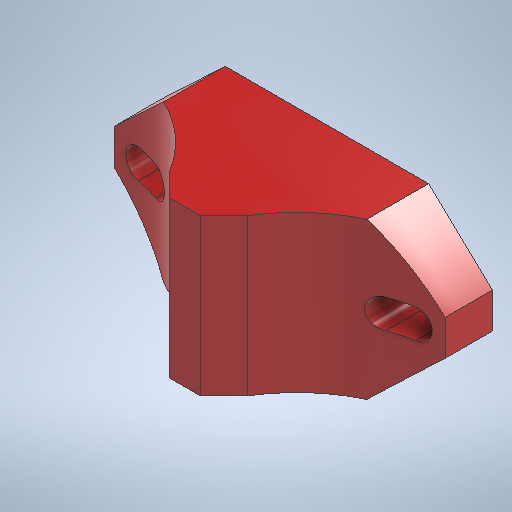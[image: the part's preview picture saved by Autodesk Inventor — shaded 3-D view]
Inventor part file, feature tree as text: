
AUTODESK INVENTOR PART (.ipt)
format: ipt  version: 2025.1 (Build 291241000, 241)  size: 330,240 bytes
history: native  units: in
note: dims shown in document units (in); Inventor stores cm internally (conversion verified against a paired STEP export)
features: projected_geometry x10, extrude x3, sketch x3, other x1
ambient origin geometry x8: Origin, YZ Plane, XZ Plane, XY Plane, X Axis, Y Axis, Z Axis, Center Point
bodies: Solid1 (feature_tree)
feature tree (17):
  extrude  "Extrusion1"  Depth=0.2953in
  extrude  "Extrusion2"  Depth=1.2992in
  extrude  "Extrusion3"  Depth=0.2441in
  sketch  "Sketch1"  dims[d0=2.7559in d1=0.2953in]
  sketch  "Sketch2"  dims[d2=1.6929in d3=1.2992in]
  projected_geometry  "Projected Loop1"
  projected_geometry  "Projected Loop2"
  projected_geometry  "Projected Loop3"
  projected_geometry  "Projected Loop4"
  projected_geometry  "Projected Loop5"
  projected_geometry  "Projected Loop6"
  projected_geometry  "Projected Loop7"
  projected_geometry  "Projected Loop8"
  projected_geometry  "Projected Loop9"
  projected_geometry  "Projected Loop10"
  sketch  "Sketch3"  dims[d4=1.1811in d5=0.0in d6=0.128in d7=0.3937in d8=0.2756in d9=45.0deg d10=1.4311in d11=0.0in d12=0.2244in d13=0.2441in d14=0.3189in d15=0.2441in d16=1.4311in d17=0.0in]
  other  "Finish1"
